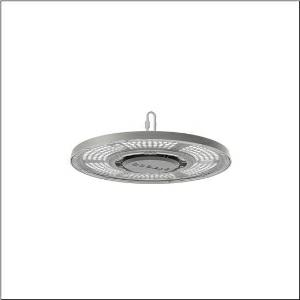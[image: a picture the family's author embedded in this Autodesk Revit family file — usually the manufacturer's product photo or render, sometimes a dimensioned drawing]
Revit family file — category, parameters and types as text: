
# Revit family: highbay_31-s_51hc427a4fmb
name_source: partatom
category: Lighting Fixtures
units: mm (PartAtom-declared; Revit-internal decimal feet)

## family parameters
Cut with Voids When Loaded = No
Host = Face
Light Source = No
Part Type = Normal
Room Calculation Point = No
Round Connector Dimension = Use Diameter
Shared = No

## types (1)
- Highbay 31-S (1 x LED, 14000 lm, 94 W, 4000K)
    Apparent Load = 94 VA
    CIE Flux Codes = 77 99 100 100 100
    Color Rendering = 80
    Color Temperature = 4000K
    Default Elevation = 1800 mm
    Description = Highbay 31-S, high bay luminaire, primary light control with lens, of PC, primary optical cover: cover panel, of PC, transparent, light emission: direct distribution, primary light characteristic: rotationally symmetric, installation type: suspended mounting, surface-mounted, LED, rated luminous flux: 14.000lm, luminous efficacy: 150lm/W, light colour: 840, colour temperature: 4000K, control gear: ON/OFF, with cable, 3x 1.0mm², free wire ends, mains connection: 220..240V, AC/DC, 0/50..60Hz, cable length: 1,5m, rated input power: 94W, housing, rotationally symmetric, of diecast aluminium, powder-coated, grey aluminium (RAL 9007), with hook on luminaire side, incl. screw, diameter: 339mm, protection rating (complete): IP65, insulation class (complete): insulation class I (protective earthing), certification: CE, ENEC, UKCA, protection symbol: D, impact resistance: IK08, permissible operating ambient temperature: -30..+45°C, standard: EN 60598-2-22, EN 60598, corresponds to IFS (International Featured Standards) requirements for safety and quality in the food industry, packaging unit: 1 piece
    Height = 141 mm
    Lamp = 1 x LED
    Lamp Light Flux = 14000 lm
    Lamp Power = 94 W
    Lamp count = 1
    Length = 339 mm
    Luminous efficacy = 149 lm/W
    Manufacturer = Siteco
    ModVariant = No
    Model = 51HC427A4FMB
    Mounting Place = Ceiling
    Mounting Type = Pendant
    Number of Poles = 1
    OnlyDefault = Yes
    Power Factor = 1
    Product Name = Highbay 31-S
    Product group = high bay luminaire
    ProductGroupID = 901
    Protection Class = Protection class I
    Protection Degree = IP 65
    RLX_Detail_Level = 1
    RLX_Emergency_Light_Flux = 0 lm
    RLX_Emergency_Type = 0
    RLX_Emergency_Type_DB = No
    RlxData = <blob elided: 162645 chars, md5=f11baffd>
    Socket = socket
    Standby Power = 0 W
    System Light Flux = 14000 lm
    System Power = 94 W
    Type Comments = Product without accessories
    Type Image = l_1007237.jpg
    URL = http://relux.com
    VarID = ---
    Voltage = 0 V
    Weight = 0.00 kg
    Width = 0 mm  [stored 0 ft]

note: [stored X ft] marks values corroborated as IEEE doubles in the binary element streams (Revit-internal decimal feet)

## geometry (parser evidence)
native form markers: Blend x4, Sweep x9
no freeform markers — native parametric forms only
